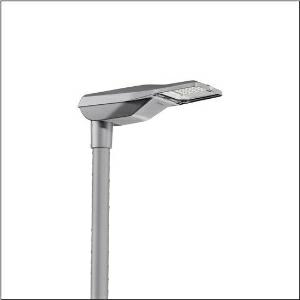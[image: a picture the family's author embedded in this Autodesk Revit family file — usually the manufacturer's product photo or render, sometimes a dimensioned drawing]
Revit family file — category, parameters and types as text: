
# Revit family: streetlight_sl_21_iq_micro___st0_8a_5xe1c31g08cb_6ed2
name_source: partatom
category: Lighting Fixtures
units: mm (PartAtom-declared; Revit-internal decimal feet)

## family parameters
Cut with Voids When Loaded = No
Host = Face
Light Source = No
Part Type = Normal
Room Calculation Point = No
Round Connector Dimension = Use Diameter
Shared = No

## types (1)
- --- (1 x LED, 2870 lm, 19.4 W, 3000K)
    Apparent Load = 19 VA
    CIE Flux Codes = 38 75 97 100 100
    Color Rendering = 70
    Color Temperature = 3000K
    Default Elevation = 1800 mm
    Description = Streetlight SL 21 iQ micro, mast luminaire, primary light control with lens, of PMMA, primary optical cover: cover, of toughened safety glass, transparent, light distribution: ST0.8a, light emission: direct distribution, primary light characteristic: asymmetric, installation type: post-top, side-entry, LED, High Power LED, rated luminous flux: 2.870lm, luminous efficacy: 148lm/W, light colour: 730, colour temperature: 3000K, control gear: iQ Street-Remote, control: Street-Remote, Auto-Match, Temp-Guard, Lumen-Switch, Night-Set, Smart-Wire, Light-Fading, Desk-Remote (wireless, voltage-free reading and setting of iQ features in the workshop via application-optimized NFC function/RFID function), optimised constant luminous flux control (CLO 2.0), pre-setting: linear dimming characteristic, mains connection: 220..240V, AC, 50/60Hz, start of lifetime: 19W, end of service life: 20W, reduction: 10W, luminaire housing, of diecast aluminium, powder-coated, SITECO metallic grey (DB 702S), corrosivity category C5 high according to DIN EN ISO 12944, please order mast flange separately, inclination adjustable: 0°, 5°, 10°, 15°, sealing non-destructively replaceable, multi-level sealing system, length: 528mm, width: 235mm, height: 110mm, mast flange for spigot size: 42mm (side-entry): 5XC10008XM4, 60/48mm (side-entry/post-top): 5XC10108XM2, 76/60mm (side-entry/post-top): 5XC10108XM1, protection rating (complete): IP66, insulation class (complete): insulation class II (safety insulation), certification: CE, ENEC, ENEC+, VDE, impact resistance: IK10, permissible operating ambient temperature for outdoor applications: -40..+50°C, standard-compliant lighting for roads and squares, packaging unit: 1 piece

Light Distribution: ST0.8a
    Height = 110 mm
    Lamp = 1 x LED
    Lamp Light Flux = 2870 lm
    Lamp Power = 19.4 W
    Lamp count = 1
    Length = 528 mm
    Luminous efficacy = 148 lm/W
    Manufacturer = Siteco
    ModVariant = No
    Model = 5XE1C31G08CB
    Number of Poles = 1
    OnlyDefault = Yes
    Power Factor = 1
    Product Name = Streetlight SL 21 iQ micro | ST0.8a
    Product group = mast luminaire | pylon top
    ProductGroupID = 6100
    Protection Class = Protection class II
    Protection Degree = IP 66
    RLX_Detail_Level = 1
    RLX_Emergency_Light_Flux = 0 lm
    RLX_Emergency_Type = 0
    RLX_Emergency_Type_DB = No
    RlxData = <blob elided: 98973 chars, md5=ae2bc3ca>
    Socket = socket
    Standby Power = 0 W
    System Light Flux = 2870 lm
    System Power = 19 W
    Type Comments = factory setting: luminous flux: 100 % | dim-lin: 254 | 387 mA
    Type Image = l_1006881.jpg
    URL = http://relux.com
    VarID = @adj_137923
    Voltage = 0 V
    Weight = 0.00 kg
    Width = 235 mm

## geometry (parser evidence)
native form markers: Blend x4, Sweep x11
no freeform markers — native parametric forms only
